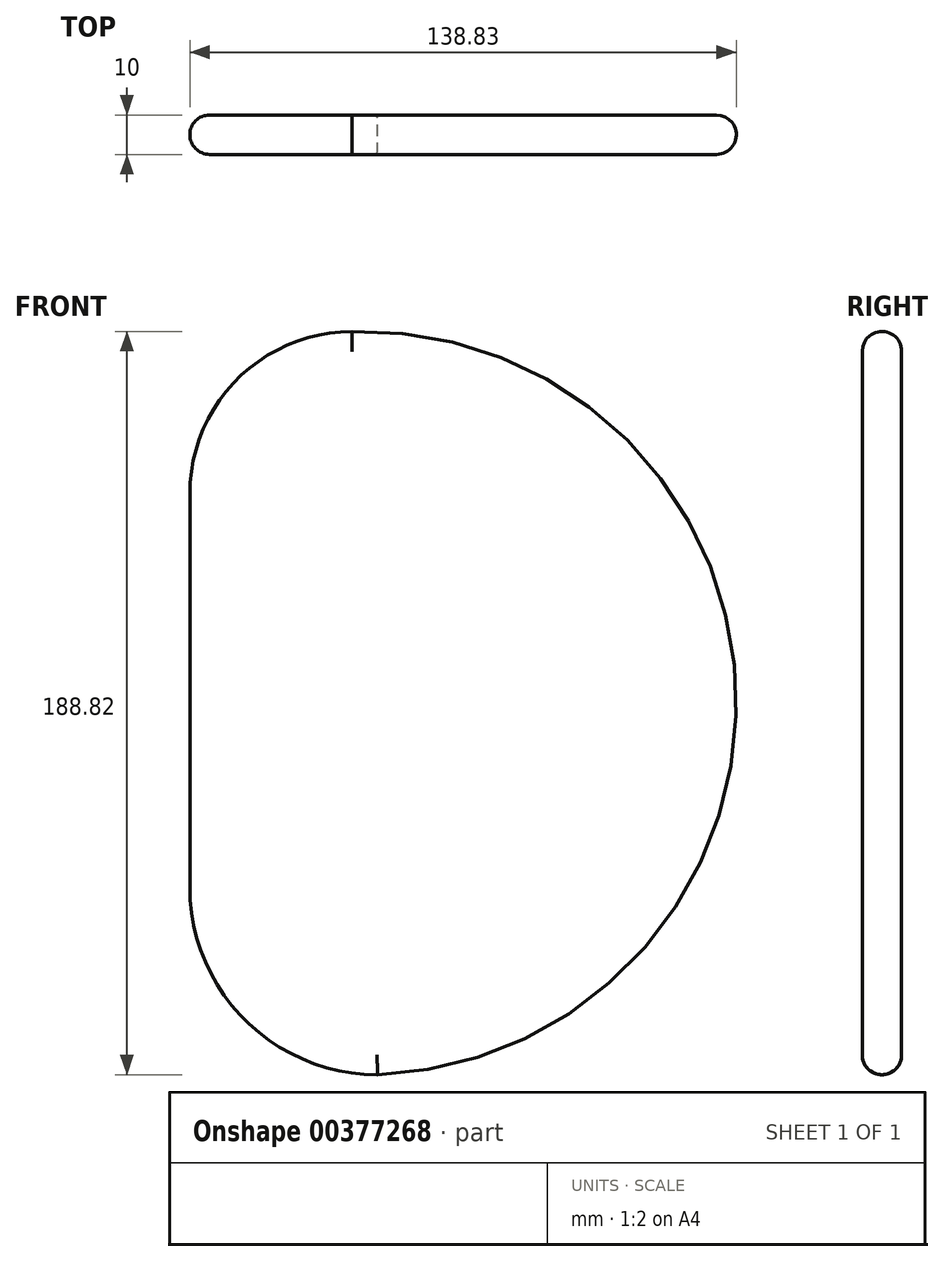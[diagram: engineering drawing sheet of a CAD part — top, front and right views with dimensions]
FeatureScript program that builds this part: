
annotation { "Feature Type Name" : "Feature", "Feature Type Description" : "" }
export const myFeature = defineFeature(function(context is Context, id is Id, definition is map)
    precondition{}
    {
        {
            var Q0;
            Q0=qCreatedBy(makeId("Front.planeOp"),FACE);
            var sketch = newSketch(context, id + "F0", { "sketchPlane" : qUnion([Q0])});
            skCircle(sketch, "E0", {"center": v(-6.48, 100) * mm, "radius": 22.23 * mm});
            skCircle(sketch, "E1", {"center": v(0, 0) * mm, "radius": 22.23 * mm});
            skArc(sketch, "E2", {"start": v(-47.63, 100) * mm, "mid": v(-35.57, 129.1) * mm, "end": v(-6.48, 141.15) * mm});
            skLineSegment(sketch, "E3", {"start": v(-47.63, 100) * mm, "end": v(-47.62, 0) * mm});
            skArc(sketch, "E4", {"start": v(-47.62, 0) * mm, "mid": v(-33.68, -33.68) * mm, "end": v(0, -47.62) * mm});
            skArc(sketch, "E5", {"start": v(-6.48, 141.15) * mm, "mid": v(91.15, 50) * mm, "end": v(0, -47.62) * mm});
            skSolve(sketch);
        }
        {
            var Q0;
            Q0=makeQuery(id+"F0.imprint","IMPRINT",FACE,{"disambiguationData":[TD([[makeQuery(id+"F0.imprint","IMPRINT",EDGE,{"derivedFrom":sQuery(id+"F0.wireOp",EDGE,"E0")}),-1.0]])]});
            var Q1;
            Q1=makeQuery(id+"F0.imprint","IMPRINT",FACE,{"disambiguationData":[TD([[makeQuery(id+"F0.imprint","IMPRINT",EDGE,{"derivedFrom":sQuery(id+"F0.wireOp",EDGE,"E0")}),1.0]])]});
            var Q2;
            Q2=makeQuery(id+"F0.imprint","IMPRINT",FACE,{"disambiguationData":[TD([[makeQuery(id+"F0.imprint","IMPRINT",EDGE,{"derivedFrom":sQuery(id+"F0.wireOp",EDGE,"E1")}),1.0]])]});
            extrude(context, id + "F1", {"entities" : qUnion([Q0, Q1, Q2]), "endBound" : BoundingType.SYMMETRIC, "depth" : 10 * mm});
        }
        {
            var Q0;
            Q0=makeQuery(id+"F1.opExtrude","CAP_EDGE",EDGE,{"disambiguationData":[OSD([sQuery(id+"F0.wireOp",EDGE,"E5")])],"isStart":false});
            var Q1;
            Q1=makeQuery(id+"F1.opExtrude","CAP_EDGE",EDGE,{"disambiguationData":[OSD([sQuery(id+"F0.wireOp",EDGE,"E5")])],"isStart":true});
            fillet(context, id + "F2", {"entities" : qUnion([Q0, Q1]), "radius" : 5 * mm, "tangentPropagation" : true, "allowEdgeOverflow" : false});
        }
        {
            var Q0;
            Q0=makeQuery(id+"F1.opExtrude","CAP_EDGE",EDGE,{"disambiguationData":[OSD([sQuery(id+"F0.wireOp",EDGE,"E3")])],"isStart":false});
            fillet(context, id + "F3", {"entities" : qUnion([Q0]), "radius" : 5 * mm, "tangentPropagation" : true, "allowEdgeOverflow" : false});
        }
    });
